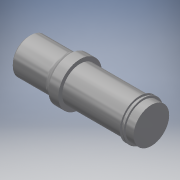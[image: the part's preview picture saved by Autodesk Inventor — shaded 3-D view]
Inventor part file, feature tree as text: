
AUTODESK INVENTOR PART (.ipt)
format: ipt  version: 2019 (Build 230136000, 136)  size: 153,600 bytes
history: native  units: mm
features: other x6, chamfer x2, fillet x1
ambient origin geometry x6: Origin, XZ Plane, XY Plane, X Axis, Y Axis, Z Axis
bodies: Body1 (feature_tree)
feature tree (9):
  other  "實體1"
  other  "迴轉1"
  chamfer  "倒角3"  [1 undecoded]
  chamfer  "倒角1"  Distance=9.0mm
  fillet  "圓角1"  Radius=11.0mm
  other  "扣環槽1"
  other  "起始平面"
  other  "主要草圖"
  other  "iFeature27:1"
note: 1 required parameter value undecoded (feature->parameter linkage not recoverable at this tier; creation-order binding heuristic only, values carry confidence <= 0.55)
